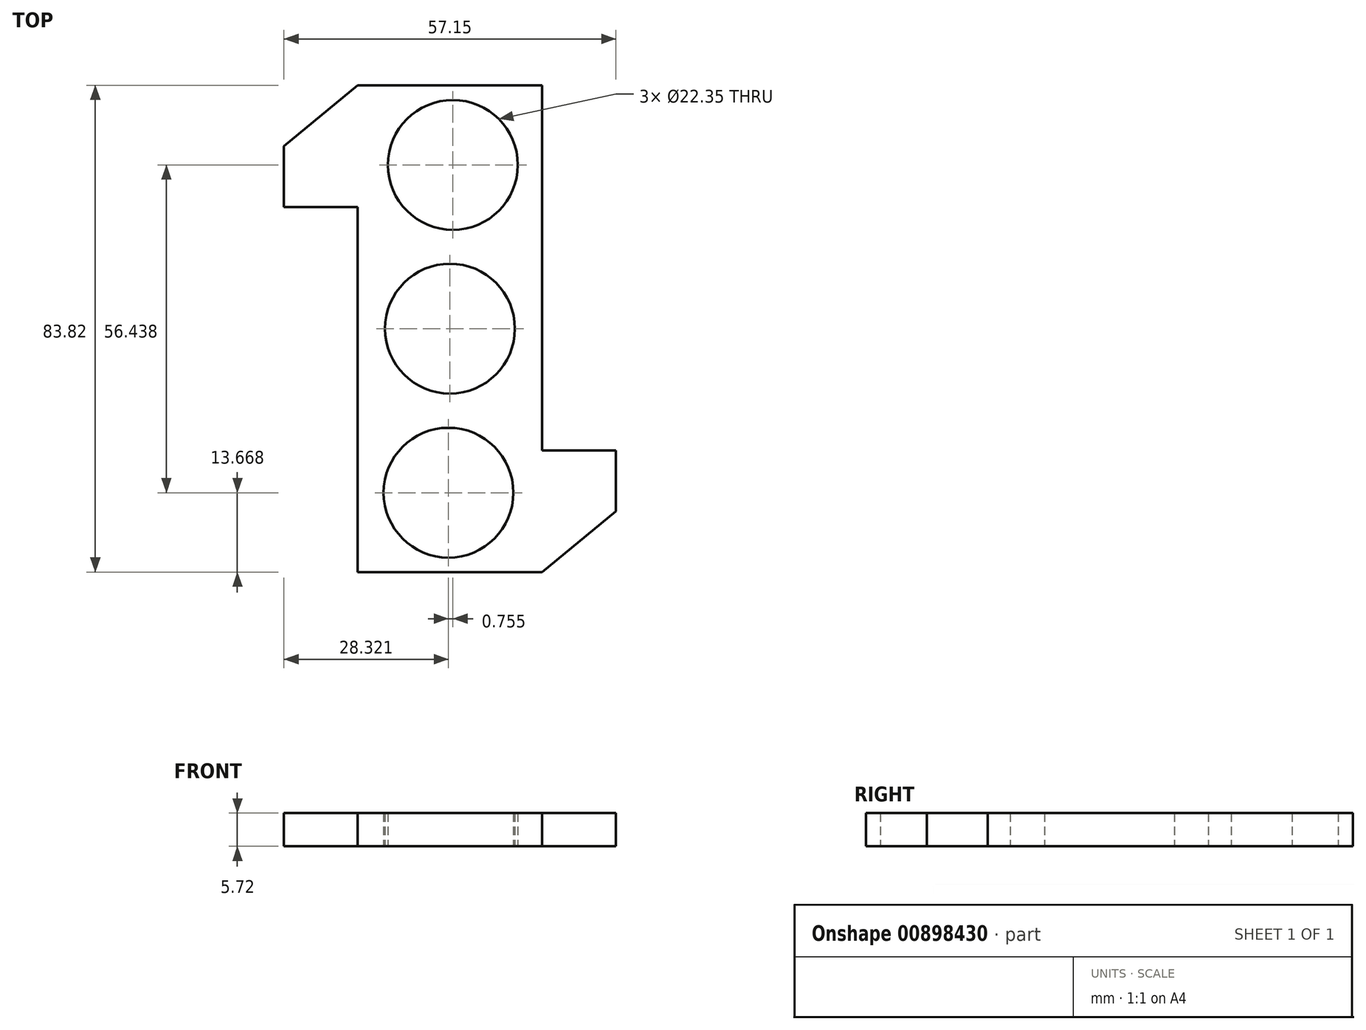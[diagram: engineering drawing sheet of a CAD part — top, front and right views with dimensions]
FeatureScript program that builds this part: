
annotation { "Feature Type Name" : "Feature", "Feature Type Description" : "" }
export const myFeature = defineFeature(function(context is Context, id is Id, definition is map)
    precondition{}
    {
        {
            var Q0;
            Q0=qCreatedBy(makeId("Top.planeOp"),FACE);
            var sketch = newSketch(context, id + "F0", { "sketchPlane" : qUnion([Q0])});
            skCircle(sketch, "E0", {"center": v(-1.1, 0.58) * mm, "radius": 11.18 * mm});
            skCircle(sketch, "E1", {"center": v(-1.1, 0.58) * mm, "radius": 15.88 * mm});
            skLineSegment(sketch, "E2", {"start": v(-16.98, 0.58) * mm, "end": v(-16.98, -41.33) * mm});
            skLineSegment(sketch, "E3", {"start": v(14.77, 0.58) * mm, "end": v(14.77, -41.33) * mm});
            skLineSegment(sketch, "E4", {"start": v(14.77, -41.33) * mm, "end": v(-16.98, -41.33) * mm});
            skLineSegment(sketch, "E5", {"start": v(-16.98, 0.58) * mm, "end": v(-16.98, 42.5) * mm});
            skLineSegment(sketch, "E6", {"start": v(14.77, 0.58) * mm, "end": v(14.77, 42.5) * mm});
            skLineSegment(sketch, "E7", {"start": v(14.77, 42.5) * mm, "end": v(-16.98, 42.5) * mm});
            skCircle(sketch, "E8", {"center": v(-0.6, 28.78) * mm, "radius": 11.18 * mm});
            skCircle(sketch, "E9", {"center": v(-1.36, -27.66) * mm, "radius": 11.18 * mm});
            skLineSegment(sketch, "E10", {"start": v(14.77, -41.33) * mm, "end": v(27.47, -30.85) * mm});
            skPoint(sketch, "E10.endSnap0", {"position": v(14.77, -20.37) * mm});
            skLineSegment(sketch, "E11", {"start": v(27.47, -20.37) * mm, "end": v(14.77, -20.37) * mm});
            skLineSegment(sketch, "E12", {"start": v(-16.98, 42.5) * mm, "end": v(-29.68, 32.02) * mm});
            skPoint(sketch, "E12.endSnap0", {"position": v(14.77, 21.54) * mm});
            skLineSegment(sketch, "E13", {"start": v(-29.68, 21.54) * mm, "end": v(-16.98, 21.54) * mm});
            skLineSegment(sketch, "E14", {"start": v(27.47, -20.37) * mm, "end": v(27.47, -30.85) * mm});
            skLineSegment(sketch, "E15", {"start": v(-29.68, 32.02) * mm, "end": v(-29.68, 21.54) * mm});
            skPoint(sketch, "E16.orphan", {"position": v(40.17, -20.37) * mm});
            skPoint(sketch, "E17.orphan", {"position": v(-42.38, 21.54) * mm});
            skSolve(sketch);
        }
        {
            var Q0;
            {var subQ1=sQuery(id+"F0.wireOp",EDGE,"E2");Q0=makeQuery(id+"F0.imprint","IMPRINT",FACE,{"disambiguationData":[TD([[makeQuery(id+"F0.imprint","IMPRINT",EDGE,{"derivedFrom":subQ1}),1.0]])]});}
            var Q1;
            Q1=makeQuery(id+"F0.imprint","IMPRINT",FACE,{"disambiguationData":[TD([[makeQuery(id+"F0.imprint","IMPRINT",EDGE,{"derivedFrom":sQuery(id+"F0.wireOp",EDGE,"E0")}),-1.0]])]});
            var Q2;
            {var subQ1=sQuery(id+"F0.wireOp",EDGE,"E5");Q2=makeQuery(id+"F0.imprint","IMPRINT",FACE,{"disambiguationData":[TD([[makeQuery(id+"F0.imprint","IMPRINT",EDGE,{"derivedFrom":subQ1}),-1.0]])]});}
            var Q3;
            {var subQ0=sQuery(id+"F0.wireOp",EDGE,"E10");Q3=makeQuery(id+"F0.imprint","IMPRINT",FACE,{"disambiguationData":[TD([[makeQuery(id+"F0.imprint","IMPRINT",EDGE,{"derivedFrom":subQ0}),1.0]])]});}
            var Q4;
            {var subQ0=sQuery(id+"F0.wireOp",EDGE,"E12");Q4=makeQuery(id+"F0.imprint","IMPRINT",FACE,{"disambiguationData":[TD([[makeQuery(id+"F0.imprint","IMPRINT",EDGE,{"derivedFrom":subQ0}),1.0]])]});}
            extrude(context, id + "F1", {"entities" : qUnion([Q0, Q1, Q2, Q3, Q4]), "depth" : 5.7 * mm, "offsetDistance" : 25.4 * mm});
        }
    });
